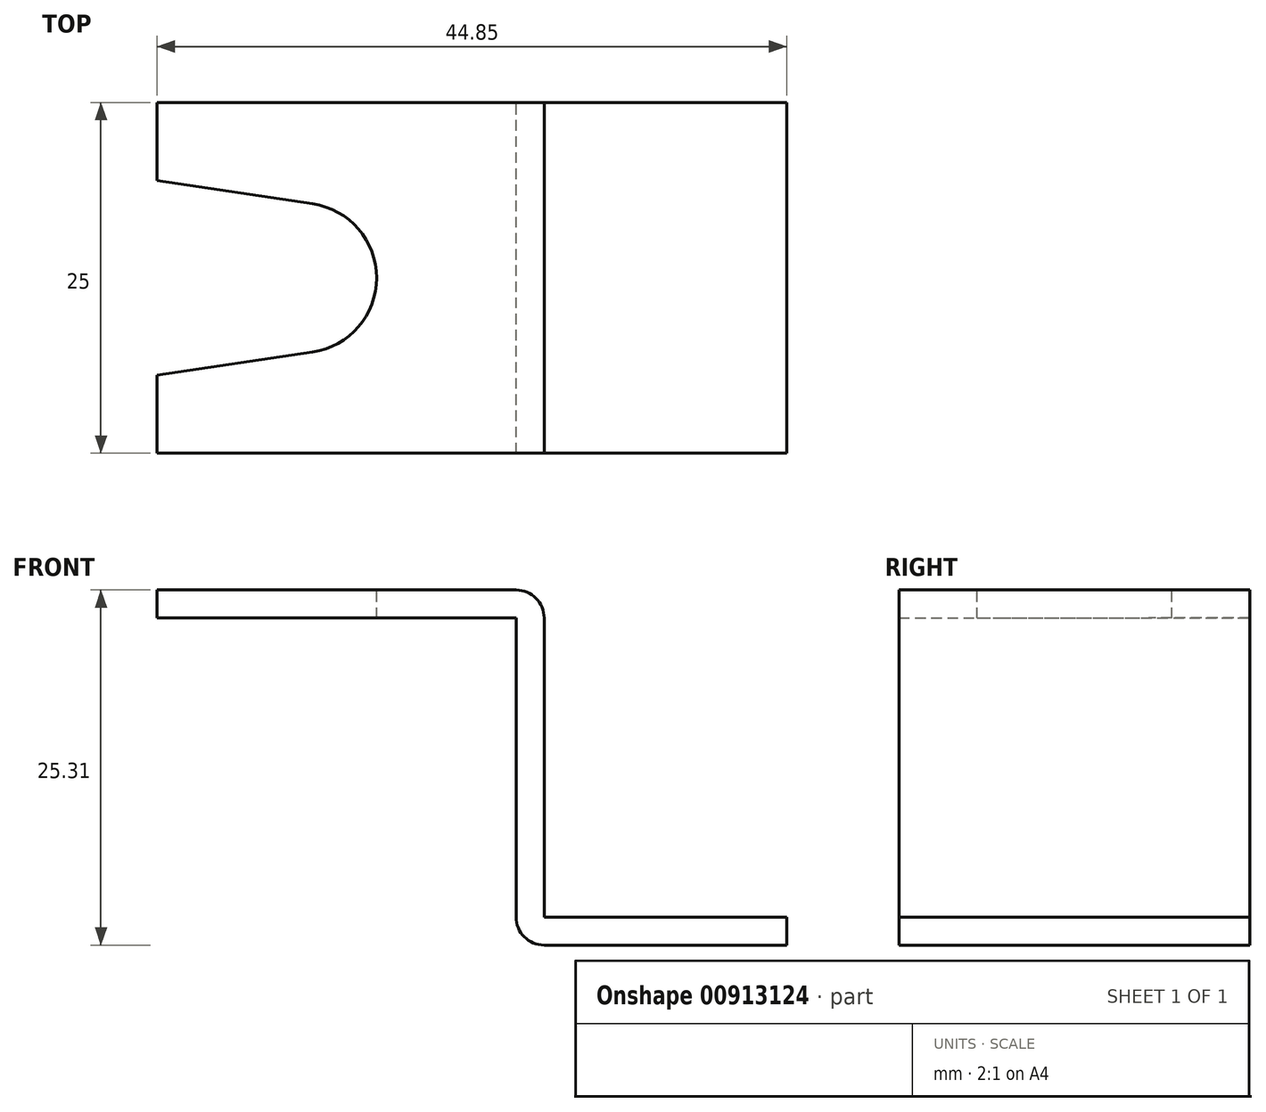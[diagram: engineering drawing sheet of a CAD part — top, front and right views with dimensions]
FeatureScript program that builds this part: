
annotation { "Feature Type Name" : "Feature", "Feature Type Description" : "" }
export const myFeature = defineFeature(function(context is Context, id is Id, definition is map)
    precondition{}
    {
        {
            var Q0;
            Q0=qCreatedBy(makeId("Front.planeOp"),FACE);
            var sketch = newSketch(context, id + "F0", { "sketchPlane" : qUnion([Q0])});
            skLineSegment(sketch, "E0", {"start": v(-58.13, 0) * mm, "end": v(-2, 0) * mm});
            skLineSegment(sketch, "E1", {"start": v(0, -2) * mm, "end": v(0, -23.3) * mm});
            skLineSegment(sketch, "E2", {"start": v(0, -23.3) * mm, "end": v(17.28, -23.3) * mm});
            skLineSegment(sketch, "E3.0", {"start": v(0, -25.3) * mm, "end": v(17.28, -25.3) * mm});
            skLineSegment(sketch, "E3.1", {"start": v(-2, -2) * mm, "end": v(-2, -23.3) * mm});
            skLineSegment(sketch, "E3.2", {"start": v(-58.13, -2) * mm, "end": v(-2, -2) * mm});
            skLineSegment(sketch, "E4", {"start": v(-58.13, 0) * mm, "end": v(-58.13, -2) * mm});
            skLineSegment(sketch, "E5", {"start": v(17.28, -23.3) * mm, "end": v(17.28, -25.3) * mm});
            skPoint(sketch, "E6.visualSharp", {"position": v(0, 0) * mm});
            skArc(sketch, "E6.filletArc", {"start": v(0, -2) * mm, "mid": v(-0.59, -0.59) * mm, "end": v(-2, 0) * mm});
            skPoint(sketch, "E7.visualSharp", {"position": v(-2, -25.3) * mm});
            skArc(sketch, "E7.filletArc", {"start": v(-2, -23.3) * mm, "mid": v(-1.41, -24.72) * mm, "end": v(0, -25.3) * mm});
            skSolve(sketch);
        }
        {
            var Q0;
            Q0=makeQuery(id+"F0.imprint","IMPRINT",FACE,{"disambiguationData":[TD([[makeQuery(id+"F0.imprint","IMPRINT",EDGE,{"derivedFrom":sQuery(id+"F0.wireOp",EDGE,"E0")}),-1.0]])]});
            extrude(context, id + "F1", {"entities" : qUnion([Q0]), "depth" : 25 * mm, "offsetDistance" : 25 * mm});
        }
        {
            var Q0;
            Q0=makeQuery(id+"F1.opExtrude","SWEPT_FACE",FACE,{"disambiguationData":[OSD([sQuery(id+"F0.wireOp",EDGE,"E0")])]});
            var sketch = newSketch(context, id + "F2", { "sketchPlane" : qUnion([Q0])});
            skCircle(sketch, "E8", {"center": v(-17.28, -12.5) * mm, "radius": 5.34 * mm});
            skLineSegment(sketch, "E9", {"start": v(-69.83, -12.5) * mm, "end": v(27.9, -12.5) * mm, "construction": true});
            skPoint(sketch, "E10", {"position": v(-14.25, -16.9) * mm});
            skPoint(sketch, "E11", {"position": v(-14.25, -8.1) * mm});
            skPoint(sketch, "E12", {"position": v(-24.86, 0) * mm});
            skPoint(sketch, "E13", {"position": v(-24.86, -25) * mm});
            skSolve(sketch);
        }
        {
            var Q0;
            {var subQ0=sQuery(id+"F2.wireOp",EDGE,"E8");var subQ1=makeQuery(id+"F2.imprint","IMPRINT",VERTEX,{"disambiguationData":[OD(0.0)],"derivedFrom":subQ0});Q0=makeQuery(id+"F2.imprint","IMPRINT",FACE,{"disambiguationData":[TD([[makeQuery(id+"F2.imprint","IMPRINT",EDGE,{"disambiguationData":[TD([[subQ1,-1.0]])],"derivedFrom":subQ0}),1.0]])]});}
            extrude(context, id + "F3", {"entities" : qUnion([Q0]), "operationType" : NewBodyOperationType.REMOVE, "endBound" : BoundingType.THROUGH_ALL, "oppositeDirection" : true, "depth" : -2 * mm, "offsetDistance" : 25 * mm});
        }
        {
            var Q0;
            Q0=makeQuery(id+"F1.opExtrude","SWEPT_FACE",FACE,{"disambiguationData":[OSD([sQuery(id+"F0.wireOp",EDGE,"E0")])]});
            var sketch = newSketch(context, id + "F4", { "sketchPlane" : qUnion([Q0])});
            skLineSegment(sketch, "E14", {"start": v(-27.57, 0) * mm, "end": v(-27.57, -5.57) * mm});
            skLineSegment(sketch, "E15", {"start": v(-27.57, -5.57) * mm, "end": v(-16.5, -7.22) * mm});
            skPoint(sketch, "E16", {"position": v(-16.5, -7.22) * mm});
            skPoint(sketch, "E17", {"position": v(-27.57, 0) * mm});
            skLineSegment(sketch, "E18", {"start": v(-65.3, -12.5) * mm, "end": v(4.5, -12.5) * mm, "construction": true});
            skLineSegment(sketch, "E19.MirrorCS", {"start": v(-27.57, -19.43) * mm, "end": v(-16.5, -17.78) * mm});
            skLineSegment(sketch, "E20.MirrorCS", {"start": v(-27.57, -25) * mm, "end": v(-27.57, -19.43) * mm});
            skSolve(sketch);
        }
        {
            var Q0;
            {var subQ3=sQuery(id+"F4.wireOp",EDGE,"E14");Q0=makeQuery(id+"F4.imprint","IMPRINT",FACE,{"disambiguationData":[TD([[makeQuery(id+"F4.imprint","IMPRINT",EDGE,{"derivedFrom":subQ3}),-1.0]])]});}
            extrude(context, id + "F5", {"entities" : qUnion([Q0]), "operationType" : NewBodyOperationType.REMOVE, "endBound" : BoundingType.THROUGH_ALL, "depth" : 2 * mm, "offsetDistance" : 25 * mm});
        }
        {
            var Q0;
            {var subQ3=sQuery(id+"F4.wireOp",EDGE,"E14");Q0=makeQuery(id+"F4.imprint","IMPRINT",FACE,{"disambiguationData":[TD([[makeQuery(id+"F4.imprint","IMPRINT",EDGE,{"derivedFrom":subQ3}),-1.0]])]});}
            extrude(context, id + "F6", {"entities" : qUnion([Q0]), "operationType" : NewBodyOperationType.REMOVE, "endBound" : BoundingType.THROUGH_ALL, "oppositeDirection" : true, "depth" : 2 * mm, "offsetDistance" : 25 * mm});
        }
    });
